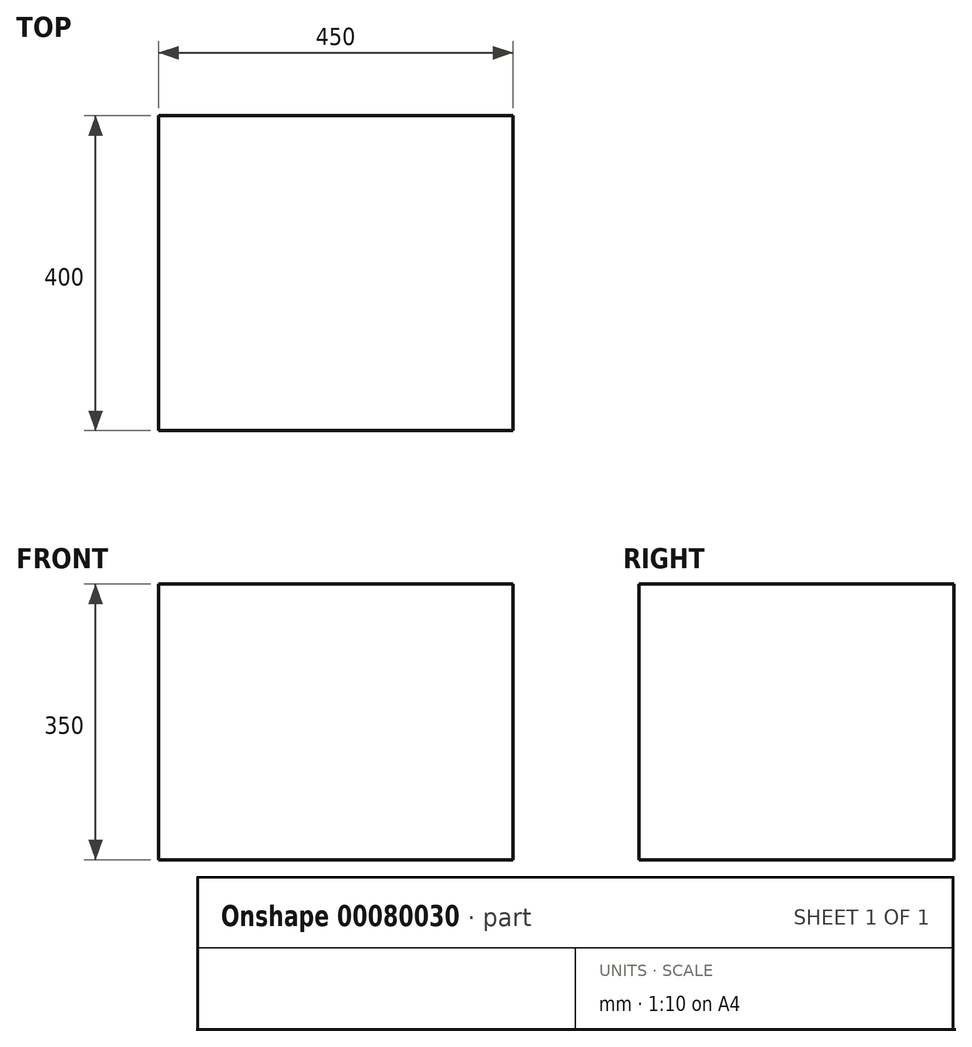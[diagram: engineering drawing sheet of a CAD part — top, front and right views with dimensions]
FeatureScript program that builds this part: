
annotation { "Feature Type Name" : "Feature", "Feature Type Description" : "" }
export const myFeature = defineFeature(function(context is Context, id is Id, definition is map)
    precondition{}
    {
        {
            var Q0;
            Q0=qCreatedBy(makeId("Front.planeOp"),FACE);
            var sketch = newSketch(context, id + "F0", { "sketchPlane" : qUnion([Q0])});
            skLineSegment(sketch, "E0.bottom", {"start": v(0, 0) * mm, "end": v(450, 0) * mm});
            skLineSegment(sketch, "E0.top", {"start": v(0, -350) * mm, "end": v(450, -350) * mm});
            skLineSegment(sketch, "E0.left", {"start": v(0, 0) * mm, "end": v(0, -350) * mm});
            skLineSegment(sketch, "E0.right", {"start": v(450, 0) * mm, "end": v(450, -350) * mm});
            skSolve(sketch);
        }
        {
            var Q0;
            Q0=makeQuery(id+"F0.imprint","IMPRINT",FACE,{"disambiguationData":[TD([[makeQuery(id+"F0.imprint","IMPRINT",EDGE,{"derivedFrom":sQuery(id+"F0.wireOp",EDGE,"E0.bottom")}),-1.0]])]});
            extrude(context, id + "F1", {"entities" : qUnion([Q0]), "oppositeDirection" : true, "depth" : 400 * mm});
        }
    });
